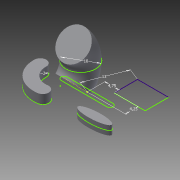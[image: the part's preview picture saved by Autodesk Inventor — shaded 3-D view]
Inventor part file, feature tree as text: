
AUTODESK INVENTOR PART (.ipt)
format: ipt  version: 2015 (Build 190159000, 159)  size: 120,320 bytes
history: native  units: mm
features: extrude x2, other x1, revolve x1
ambient origin geometry x8: Origin, YZ Plane, XZ Plane, XY Plane, X Axis, Y Axis, Z Axis, Center Point
bodies: Volumenkörper1 (feature_tree)
feature tree (4):
  other  "Demo-Sketch-01"
  extrude  "Extrusion1"  Depth=10.0mm
  extrude  "Extrusion2"  Depth=2.0mm
  revolve  "Umdrehung1"
